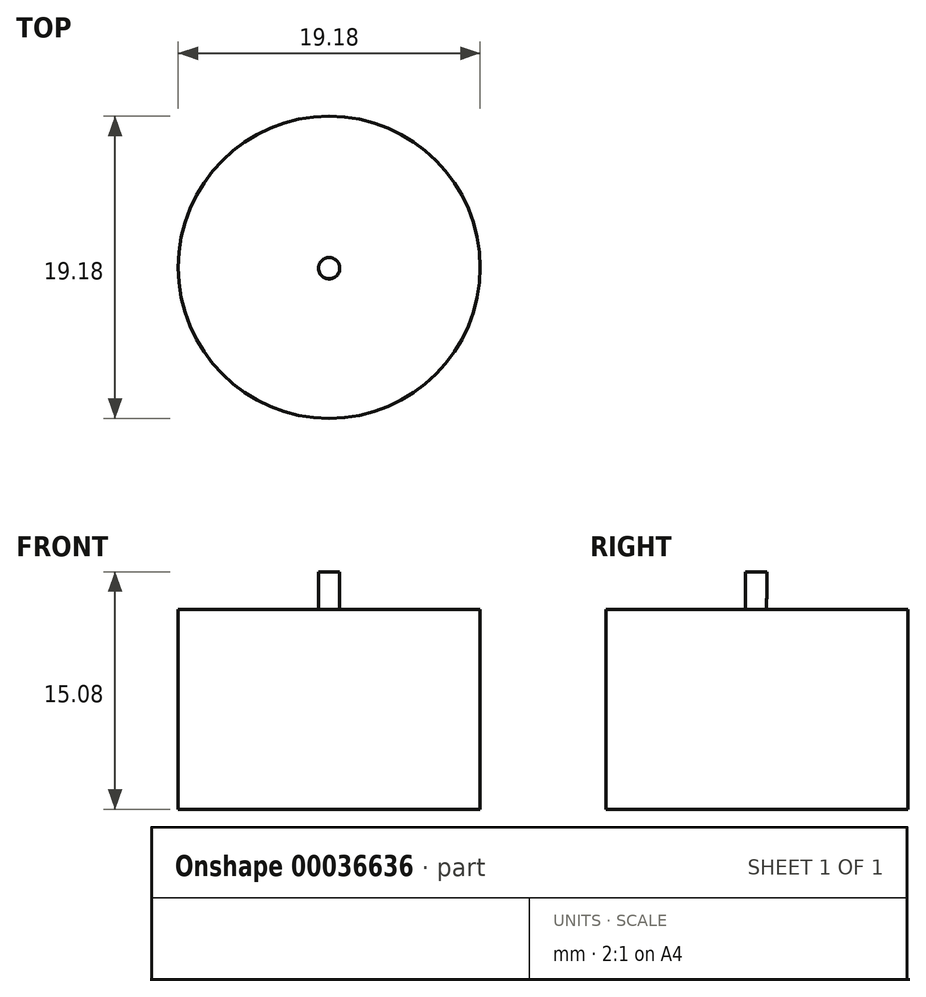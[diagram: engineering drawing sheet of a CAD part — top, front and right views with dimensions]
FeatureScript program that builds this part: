
annotation { "Feature Type Name" : "Feature", "Feature Type Description" : "" }
export const myFeature = defineFeature(function(context is Context, id is Id, definition is map)
    precondition{}
    {
        {
            var Q0;
            Q0=qCreatedBy(makeId("Top.planeOp"),FACE);
            var sketch = newSketch(context, id + "F0", { "sketchPlane" : qUnion([Q0])});
            skCircle(sketch, "E0", {"center": v(0, 0) * mm, "radius": 9.6 * mm});
            skSolve(sketch);
        }
        {
            var Q0;
            Q0=qCreatedBy(makeId("Right.planeOp"),FACE);
            var sketch = newSketch(context, id + "F1", { "sketchPlane" : qUnion([Q0])});
            skFitSpline(sketch, "E1", {"points": [v(0, 25.46) * mm, v(0, 30.36) * mm, v(1.85, 31.15) * mm], "startDerivative": vector(-1.44, 9.86) * mm, "endDerivative": vector(5.66, 0.86) * mm});
            skSolve(sketch);
        }
        {
            var Q0;
            Q0=qCreatedBy(makeId("Front.planeOp"),FACE);
            cPlane(context, id + "F2", {"entities" : qUnion([Q0]), "cplaneType" : CPlaneType.OFFSET, "offset" : 1.83 * mm, "oppositeDirection" : true, "width" : 152.4 * mm, "height" : 152.4 * mm});
        }
        {
            var Q0;
            Q0=qCreatedBy(id+"F2.planeOp",FACE);
            var sketch = newSketch(context, id + "F3", { "sketchPlane" : qUnion([Q0])});
            skCircle(sketch, "E2", {"center": v(0, 31.15) * mm, "radius": 0.67 * mm});
            skSolve(sketch);
        }
        {
            var Q0;
            Q0=makeQuery(id+"F3.imprint","IMPRINT",FACE,{"disambiguationData":[TD([[makeQuery(id+"F3.imprint","IMPRINT",EDGE,{"derivedFrom":sQuery(id+"F3.wireOp",EDGE,"E2")}),1.0]])]});
            var Q1;
            Q1=sQuery(id+"F3.wireOp",EDGE,"E2");
            var Q2;
            Q2=sQuery(id+"F1.wireOp",EDGE,"E1");
            sweep(context, id + "F4", {"profiles" : qUnion([Q0]), "surfaceProfiles" : qUnion([Q1]), "path" : qUnion([Q2])});
        }
        {
            var Q0;
            Q0 = qSketchRegion(id + "F0", true);
            extrude(context, id + "F5", {"entities" : qUnion([Q0]), "depth" : 12.7 * mm});
        }
        {
            var Q0;
            Q0=makeQuery(id+"F4.opSweep","CAP_FACE",FACE,{"disambiguationData":[OSD([sQuery(id+"F1.wireOp",VERTEX,"E1.start"),sQuery(id+"F3.wireOp",EDGE,"E2")])],"isStart":false});
            extrude(context, id + "F6", {"entities" : qUnion([Q0]), "operationType" : NewBodyOperationType.ADD, "depth" : 25.4 * mm});
        }
        {
            var Q0;
            Q0=qCreatedBy(makeId("Front.planeOp"),FACE);
            var sketch = newSketch(context, id + "F7", { "sketchPlane" : qUnion([Q0])});
            skLineSegment(sketch, "E3.bottom", {"start": v(10.01, 15.08) * mm, "end": v(-11.6, 15.08) * mm});
            skLineSegment(sketch, "E3.top", {"start": v(10.01, 33.7) * mm, "end": v(-11.6, 33.7) * mm});
            skLineSegment(sketch, "E3.left", {"start": v(10.01, 15.08) * mm, "end": v(10.01, 33.7) * mm});
            skLineSegment(sketch, "E3.right", {"start": v(-11.6, 15.08) * mm, "end": v(-11.6, 33.7) * mm});
            skSolve(sketch);
        }
        {
            var Q0;
            Q0 = qSketchRegion(id + "F7", true);
            extrude(context, id + "F8", {"entities" : qUnion([Q0]), "operationType" : NewBodyOperationType.REMOVE, "oppositeDirection" : true, "depth" : 25.4 * mm, "hasSecondDirection" : true, "secondDirectionOppositeDirection" : false, "secondDirectionDepth" : 25.4 * mm});
        }
    });
